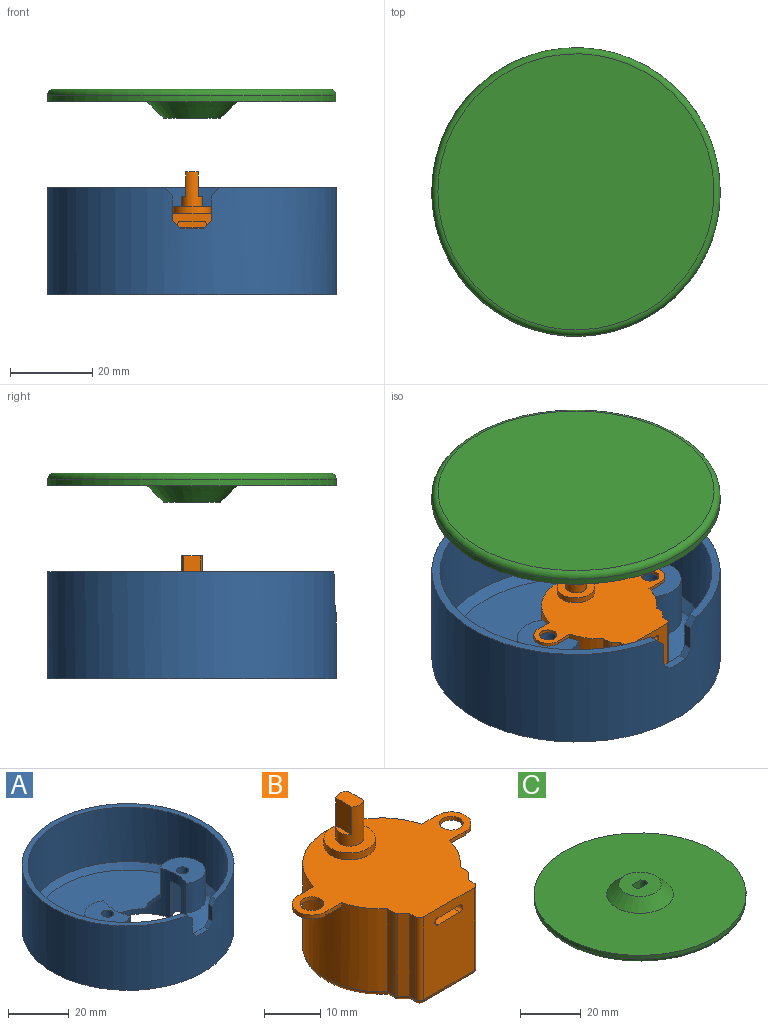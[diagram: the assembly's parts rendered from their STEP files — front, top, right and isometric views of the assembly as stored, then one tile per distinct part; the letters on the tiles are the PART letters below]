
ASSEMBLY  parts=3 mates=2
PART A: 40 faces, bbox 70x70x26 mm
  f0: plane 62x38.82mm, normal (0,0,1), area 1313.8mm2, adj f1,f31,f38,f39
  f1: cylinder r=14.5mm len=29mm, axis (0,0,-1), area 480.2mm2, adj f0,f2,f4,f5,f6,f12,f14,f15
  f2: plane 5.05x2mm, normal (-1,0,0), area 10.1mm2, adj f1,f5,f6,f37
  f3: plane 15x2mm, normal (0,1,0), area 30mm2, adj f5,f6,f36,f37
  f4: plane 5.05x2mm, normal (1,0,0), area 10.1mm2, adj f1,f5,f6,f36
  f5: plane 51.08x13.43mm, normal (0,0,1), area 260mm2, adj f1,f2,f3,f4,f31,f36,f37,f38
  f6: plane 70x70mm, normal (0,0,-1), area 3019.2mm2, adj f1,f2,f3,f4,f10,f18,f19,f20
  f7: cylinder r=33mm len=66mm, axis (0,0,-1), area 4466.2mm2, adj f8,f9,f11,f30,f31,f32,f33,f34
  f8: plane 6x2.02mm, normal (1,0,0), area 12.1mm2, adj f7,f10,f32,f35
  f9: plane 6x2.02mm, normal (-1,0,0), area 12.1mm2, adj f7,f10,f33,f34
  f10: cylinder r=35mm len=70mm, axis (0,0,-1), area 5622.4mm2, adj f6,f8,f9,f11,f30,f32,f33,f34
  f11: plane 70x69.34mm, normal (0,0,1), area 400.1mm2, adj f7,f10,f32,f33
  f12: cylinder r=7.5mm len=15mm, axis (0,0,-1), area 394.1mm2, adj f1,f14,f38
  f13: cylinder r=2mm len=4mm, axis (0,0,-1), area 50.3mm2, adj f14,f29
  f14: plane 15x11.85mm, normal (0,0,1), area 126.1mm2, adj f1,f12,f13
  f15: cylinder r=7.5mm len=15mm, axis (0,0,-1), area 394.1mm2, adj f1,f17,f39
  f16: cylinder r=2mm len=4mm, axis (0,0,-1), area 50.3mm2, adj f17,f23
  f17: plane 15x11.85mm, normal (0,0,1), area 126.1mm2, adj f1,f15,f16
  f18: plane 15x3.19mm, normal (-0.5,-0.87,0), area 55.2mm2, adj f1,f6,f19,f23
  f19: plane 15x3.6mm, normal (0.5,-0.87,0), area 62.4mm2, adj f6,f18,f20,f23
  f20: plane 15x4.16mm, normal (1,0,0), area 62.4mm2, adj f6,f19,f21,f23
  f21: plane 15x3.6mm, normal (0.5,0.87,0), area 62.4mm2, adj f6,f20,f22,f23
  f22: plane 15x3.19mm, normal (-0.5,0.87,0), area 55.2mm2, adj f1,f6,f21,f23
  f23: plane 8.31x6.79mm, normal (0,0,-1), area 29.9mm2, adj f1,f16,f18,f19,f20,f21,f22
  f24: plane 15x3.19mm, normal (0.5,0.87,0), area 55.2mm2, adj f1,f6,f25,f29
  f25: plane 15x3.6mm, normal (-0.5,0.87,0), area 62.4mm2, adj f6,f24,f26,f29
  f26: plane 15x4.16mm, normal (-1,0,0), area 62.4mm2, adj f6,f25,f27,f29
  f27: plane 15x3.6mm, normal (-0.5,-0.87,0), area 62.4mm2, adj f6,f26,f28,f29
  f28: plane 15x3.19mm, normal (0.5,-0.87,0), area 55.2mm2, adj f1,f6,f27,f29
  f29: plane 8.31x6.79mm, normal (0,0,-1), area 29.9mm2, adj f1,f13,f24,f25,f26,f27,f28
  f30: plane 5.5x2.11mm, normal (0,0,1), area 11mm2, adj f7,f10,f34,f35
  f31: cone r=31mm half-angle=45deg, axis (0,0,1), area 561.1mm2, adj f0,f5,f7,f38,f39
  f32: plane 2.38x2.01mm, normal (0.71,0,0.71), area 5.7mm2, adj f7,f8,f10,f11
  f33: plane 2.38x2.01mm, normal (-0.71,0,0.71), area 5.7mm2, adj f7,f9,f10,f11
  f34: plane 2.24x2mm, normal (-0.71,0,0.71), area 5.7mm2, adj f7,f9,f10,f30
  f35: plane 2.24x2mm, normal (0.71,0,0.71), area 5.7mm2, adj f7,f8,f10,f30
  f36: plane 2x2mm, normal (0.71,0.71,0), area 5.7mm2, adj f3,f4,f5,f6
  f37: plane 2x2mm, normal (-0.71,0.71,0), area 5.7mm2, adj f2,f3,f5,f6
  f38: cone r=7.5mm half-angle=45deg, axis (0,0,-1), area 303.4mm2, adj f0,f1,f5,f12,f31
  f39: cone r=7.5mm half-angle=45deg, axis (0,0,-1), area 303.4mm2, adj f0,f1,f5,f15,f31
PART B: 49 faces, bbox 42x32x29 mm
  f0: cylinder r=0.75mm len=2mm, axis (0,-1,0), area 4.7mm2, adj f16,f46,f47,f48
  f1: cylinder r=2.1mm len=4.2mm, axis (0,0,1), area 10.8mm2, adj f11,f44
  f2: cylinder r=2.1mm len=4.2mm, axis (0,0,1), area 10.8mm2, adj f11,f40
  f3: cylinder r=2.5mm len=8.5mm, axis (0,0,-1), area 77.9mm2, adj f5,f6,f7,f8,f9,f10
  f4: cylinder r=4.57mm len=9.14mm, axis (0,0,-1), area 43.1mm2, adj f6,f11
  f5: plane 4x1mm, normal (0,0,1), area 2.8mm2, adj f3,f9
  f6: plane 9.14x9.14mm, normal (0,0,1), area 46mm2, adj f3,f4
  f7: plane 4x1mm, normal (0,0,1), area 2.8mm2, adj f3,f8
  f8: plane 6x4mm, normal (-1,0,0), area 24mm2, adj f3,f7,f10
  f9: plane 6x4mm, normal (1,0,0), area 24mm2, adj f3,f5,f10
  f10: plane 5x3mm, normal (0,0,1), area 14mm2, adj f3,f8,f9
  f11: plane 42x30.89mm, normal (0,0,1), area 671.7mm2, adj f1,f2,f4,f12,f13,f14,f15,f16
  f12: cylinder r=1mm len=18mm, axis (0,0,1), area 14.1mm2, adj f11,f13,f23,f35
  f13: plane 18x1.48mm, normal (0.71,-0.71,0), area 37.5mm2, adj f11,f12,f14,f36
  f14: plane 18x1.5mm, normal (1,0,0), area 27mm2, adj f11,f13,f15,f34
  f15: cylinder r=1mm len=18mm, axis (0,0,1), area 28.3mm2, adj f11,f14,f16,f32
  f16: plane 18x12.7mm, normal (0,-1,0), area 218.6mm2, adj f0,f11,f15,f17,f30,f45,f46,f47
  f17: cylinder r=1mm len=18mm, axis (0,0,1), area 28.3mm2, adj f11,f16,f18,f28
  f18: plane 18x1.5mm, normal (-1,0,0), area 27mm2, adj f11,f17,f19,f26
  f19: plane 18x1.48mm, normal (-0.71,-0.71,0), area 37.5mm2, adj f11,f18,f20,f25
  f20: cylinder r=1mm len=18mm, axis (0,0,1), area 14.1mm2, adj f11,f19,f21,f27
  f21: plane 18x1.59mm, normal (-1,0,0), area 28.5mm2, adj f11,f20,f22,f29
  f22: cylinder r=14mm len=28mm, axis (0,0,1), area 1214.3mm2, adj f11,f21,f23,f31,f37,f39,f40,f41
  f23: plane 18x1.59mm, normal (1,0,0), area 28.5mm2, adj f11,f12,f22,f33
  f24: plane 28.89x26mm, normal (0,0,-1), area 582.6mm2, adj f25,f26,f29,f30,f31,f33,f34,f36
  f25: cylinder r=1mm len=2.48mm, axis (-0.71,0.71,0), area 3.6mm2, adj f19,f24,f26,f27
  f26: cylinder r=1mm len=1.91mm, axis (0,1,0), area 2.7mm2, adj f18,f24,f25,f28
  f27: sphere r=1mm, area 0.8mm2, adj f20,f25,f29
  f28: sphere r=1mm, area 1.6mm2, adj f17,f26,f30
  f29: cylinder r=1mm len=2.06mm, axis (0,1,0), area 2.9mm2, adj f21,f24,f27,f31
  f30: cylinder r=1mm len=12.7mm, axis (-1,0,0), area 19.9mm2, adj f16,f24,f28,f32
  f31: torus R=13mm, axis (0,0,1), area 104.9mm2, adj f22,f24,f29,f33
  f32: sphere r=1mm, area 1.6mm2, adj f15,f30,f34
  f33: cylinder r=1mm len=2.06mm, axis (0,-1,0), area 2.9mm2, adj f23,f24,f31,f35
  f34: cylinder r=1mm len=1.91mm, axis (0,-1,0), area 2.7mm2, adj f14,f24,f32,f36
  f35: sphere r=1mm, area 0.8mm2, adj f12,f33,f36
  f36: cylinder r=1mm len=2.48mm, axis (-0.71,-0.71,0), area 3.6mm2, adj f13,f24,f34,f35
  f37: plane 3.94x0.82mm, normal (0,1,0), area 3.2mm2, adj f11,f22,f38,f40
  f38: cylinder r=3.5mm len=7mm, axis (0,0,1), area 9mm2, adj f11,f37,f39,f40
  f39: plane 3.94x0.82mm, normal (0,-1,0), area 3.2mm2, adj f11,f22,f38,f40
  f40: plane 7.44x7mm, normal (0,0,-1), area 30.9mm2, adj f2,f22,f37,f38,f39
  f41: plane 3.94x0.82mm, normal (0,-1,0), area 3.2mm2, adj f11,f22,f42,f44
  f42: cylinder r=3.5mm len=7mm, axis (0,0,1), area 9mm2, adj f11,f41,f43,f44
  f43: plane 3.94x0.82mm, normal (0,1,0), area 3.2mm2, adj f11,f22,f42,f44
  f44: plane 7.44x7mm, normal (0,0,-1), area 30.9mm2, adj f1,f22,f41,f42,f43
  f45: cylinder r=0.75mm len=2mm, axis (0,-1,0), area 4.7mm2, adj f16,f46,f47,f48
  f46: plane 5.5x2mm, normal (0,0,-1), area 11mm2, adj f0,f16,f45,f48
  f47: plane 5.5x2mm, normal (0,0,1), area 11mm2, adj f0,f16,f45,f48
  f48: plane 7x1.5mm, normal (0,-1,0), area 10mm2, adj f0,f45,f46,f47
PART C: 11 faces, bbox 75.8x75.8x7 mm
  f0: cylinder r=35mm len=70mm, axis (0,0,-1), area 329.9mm2, adj f1,f9
  f1: plane 70x70mm, normal (0,0,1), area 3468.3mm2, adj f0,f10
  f2: plane 67x67mm, normal (0,0,-1), area 3525.7mm2, adj f9
  f3: cylinder r=2.5mm len=6mm, axis (0,0,-1), area 20.1mm2, adj f4,f6,f7,f8
  f4: plane 6x3.92mm, normal (0,1,0), area 23.5mm2, adj f3,f5,f7,f8
  f5: cylinder r=2.5mm len=6mm, axis (0,0,-1), area 20.1mm2, adj f4,f6,f7,f8
  f6: plane 6x3.92mm, normal (0,-1,0), area 23.5mm2, adj f3,f5,f7,f8
  f7: plane 14x14mm, normal (0,0,1), area 139.5mm2, adj f3,f4,f5,f6,f10
  f8: plane 5x3.1mm, normal (0,0,1), area 14.4mm2, adj f3,f4,f5,f6
  f9: torus R=33.5mm, axis (0,0,1), area 510.1mm2, adj f0,f2
  f10: cone r=6mm half-angle=45deg, axis (0,0,-1), area 319.9mm2, adj f1,f7
PLACE A t=(11.05,17.13,-5.12)mm
PLACE B t=(11.05,25.13,14.7)mm
PLACE C rot(axis=(0,1,0),180deg) t=(11.05,17.13,44.76)mm
MATE slider C.f0 <-> A.f7  axis (0,0,-1) through (11.05,25.13,41.76)mm
MATE fastened B.f1 <-> A.f16  axis (0,0,-1) through (-6.45,17.13,13.88)mm
